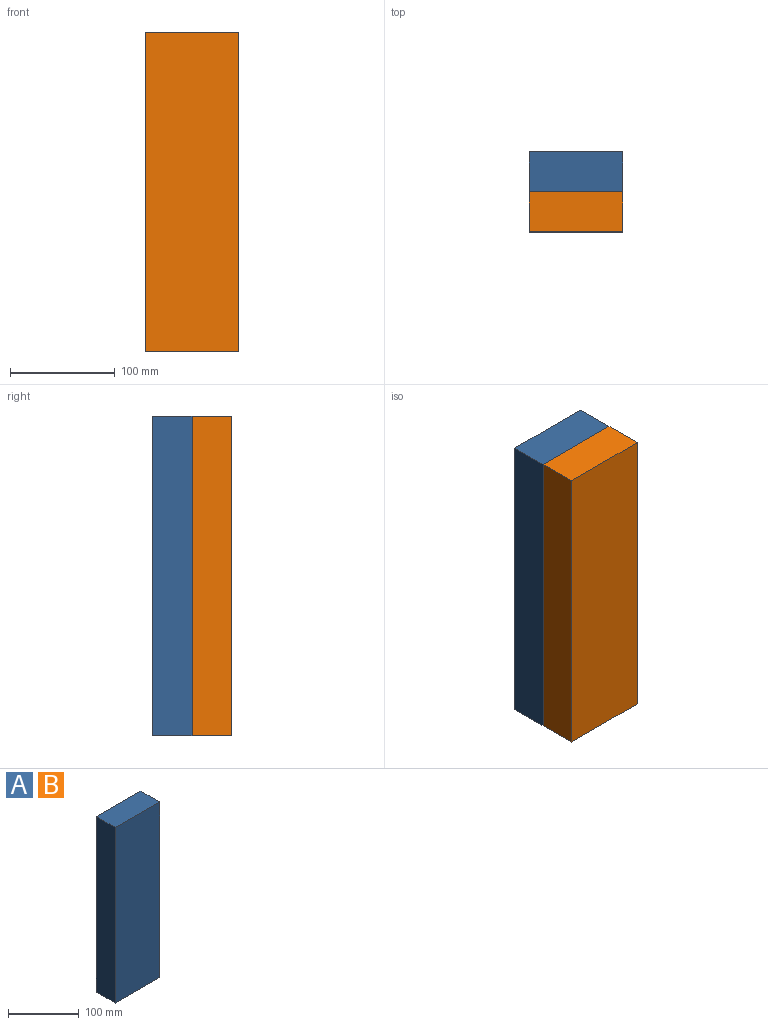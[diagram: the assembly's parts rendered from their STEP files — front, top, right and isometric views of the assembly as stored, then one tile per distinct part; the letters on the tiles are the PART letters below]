
ASSEMBLY  parts=2 mates=1
PART A: 6 faces, bbox 88.9x38.1x304.8 mm
  f0: plane 304.8x88.9mm, normal (0,-1,0), area 27096.7mm2, adj f1,f3,f4,f5
  f1: plane 304.8x38.1mm, normal (1,0,0), area 11612.9mm2, adj f0,f2,f4,f5
  f2: plane 304.8x88.9mm, normal (0,1,0), area 27096.7mm2, adj f1,f3,f4,f5
  f3: plane 304.8x38.1mm, normal (-1,0,0), area 11612.9mm2, adj f0,f2,f4,f5
  f4: plane 88.9x38.1mm, normal (0,0,1), area 3387.1mm2, adj f0,f1,f2,f3
  f5: plane 88.9x38.1mm, normal (0,0,-1), area 3387.1mm2, adj f0,f1,f2,f3
PART B: same geometry as A
PLACE A t=(0,19.05,0)mm
PLACE B t=(0,-19.05,0)mm
MATE fastened A.f0 <-> B.f2  axis (0,-1,0) through (0,0,152.4)mm
